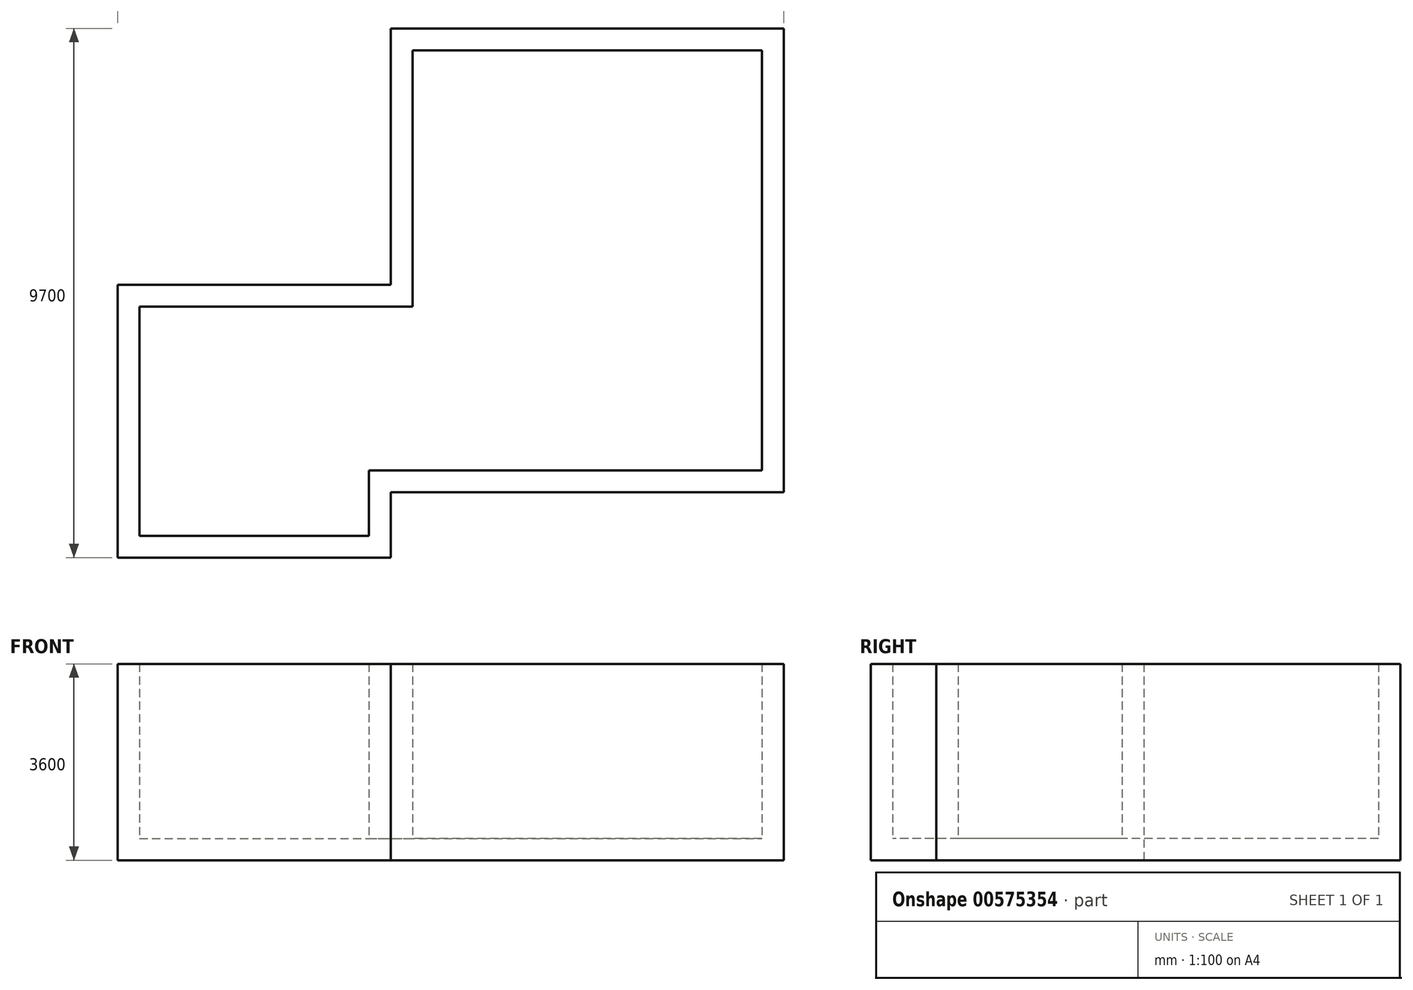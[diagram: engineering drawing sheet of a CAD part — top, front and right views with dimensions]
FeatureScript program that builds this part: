
annotation { "Feature Type Name" : "Feature", "Feature Type Description" : "" }
export const myFeature = defineFeature(function(context is Context, id is Id, definition is map)
    precondition{}
    {
        {
            var Q0;
            Q0=qCreatedBy(makeId("Top.planeOp"),FACE);
            var sketch = newSketch(context, id + "F0", { "sketchPlane" : qUnion([Q0])});
            skLineSegment(sketch, "E0.bottom", {"start": v(-2500, 2500) * mm, "end": v(2500, 2500) * mm});
            skLineSegment(sketch, "E0.top", {"start": v(-2500, -2500) * mm, "end": v(2500, -2500) * mm});
            skLineSegment(sketch, "E0.left", {"start": v(-2500, 2500) * mm, "end": v(-2500, -2500) * mm});
            skLineSegment(sketch, "E0.right", {"start": v(2500, -1300) * mm, "end": v(2500, -2500) * mm});
            skPoint(sketch, "E0.middle", {"position": v(0, 0) * mm});
            skPoint(sketch, "E1", {"position": v(2500, -1300) * mm});
            skPoint(sketch, "E2", {"position": v(9700, -1300) * mm});
            skPoint(sketch, "E3", {"position": v(2500, 2500) * mm});
            skPoint(sketch, "E4", {"position": v(2500, 7200) * mm});
            skPoint(sketch, "E5", {"position": v(9700, 7200) * mm});
            skLineSegment(sketch, "E6", {"start": v(2500, -1300) * mm, "end": v(9700, -1300) * mm});
            skLineSegment(sketch, "E7", {"start": v(9700, 7200) * mm, "end": v(2500, 7200) * mm});
            skLineSegment(sketch, "E8", {"start": v(2500, 7200) * mm, "end": v(2500, 2500) * mm});
            skLineSegment(sketch, "E9", {"start": v(9700, 7200) * mm, "end": v(9700, -1300) * mm});
            skSolve(sketch);
        }
        {
            var Q0;
            Q0=qSketchRegion(id+"F0",true);
            extrude(context, id + "F1", {"entities" : qUnion([Q0]), "depth" : 3600 * mm});
        }
        {
            var Q0;
            Q0=makeQuery(id+"F1.opExtrude","CAP_FACE",FACE,{"disambiguationData":[OSD([sQuery(id+"F0.wireOp",EDGE,"E0.bottom"),sQuery(id+"F0.wireOp",EDGE,"E0.top"),sQuery(id+"F0.wireOp",EDGE,"E0.left"),sQuery(id+"F0.wireOp",EDGE,"E0.right"),sQuery(id+"F0.wireOp",EDGE,"E6"),sQuery(id+"F0.wireOp",EDGE,"E7"),sQuery(id+"F0.wireOp",EDGE,"E8"),sQuery(id+"F0.wireOp",EDGE,"E9")])],"isStart":false});
            shell(context, id + "F2", {"entities" : qUnion([Q0]), "thickness" : 400 * mm});
        }
    });
